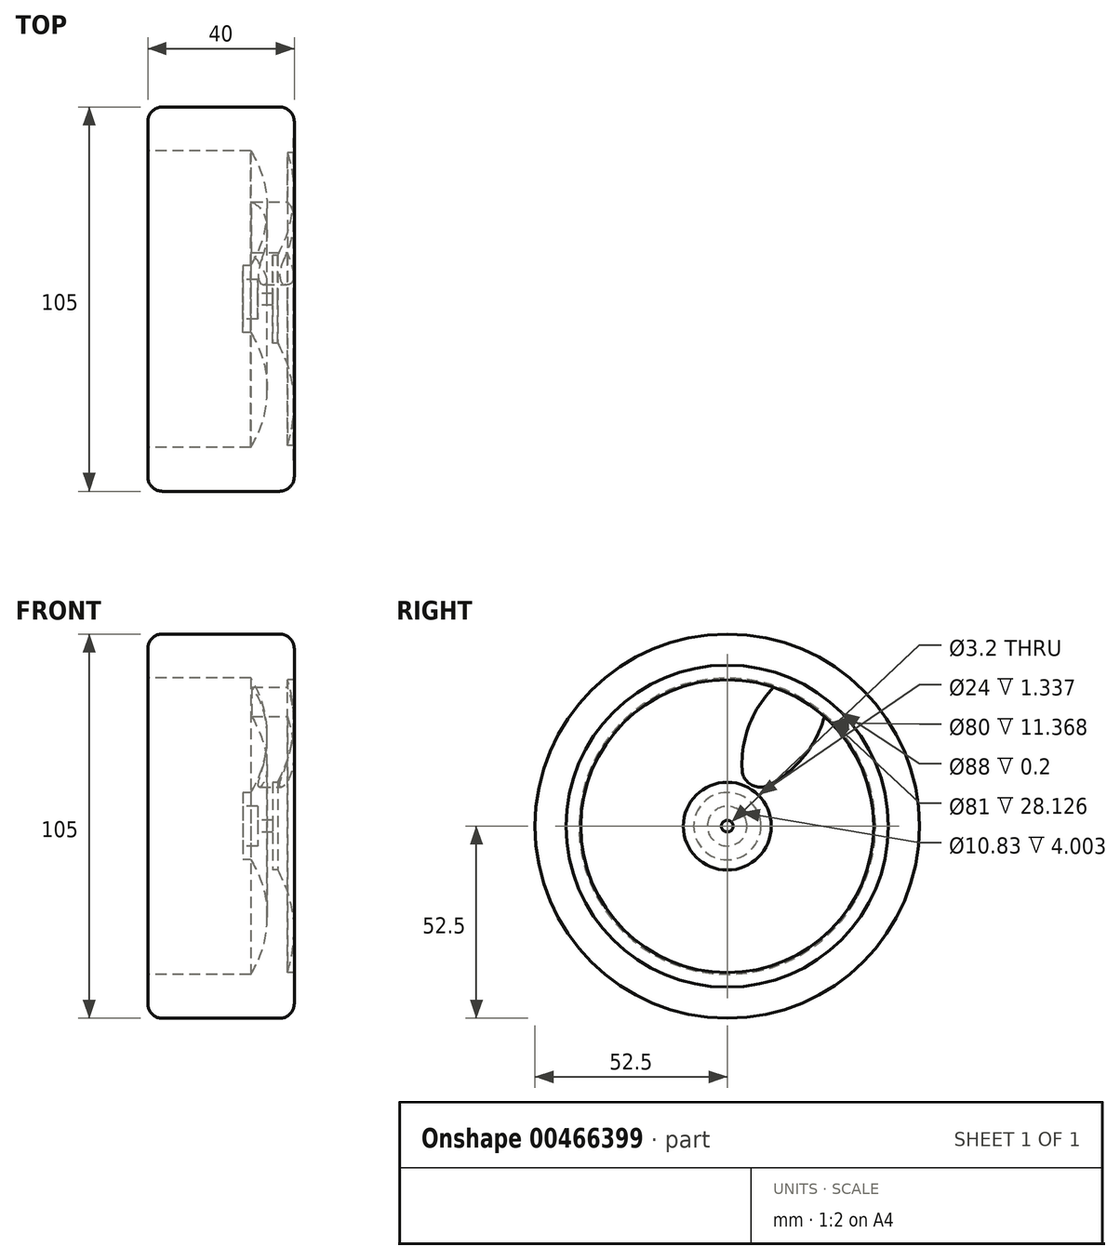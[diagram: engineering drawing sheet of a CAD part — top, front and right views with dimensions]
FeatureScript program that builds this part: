
annotation { "Feature Type Name" : "Feature", "Feature Type Description" : "" }
export const myFeature = defineFeature(function(context is Context, id is Id, definition is map)
    precondition{}
    {
        {
            var Q0;
            Q0=qCreatedBy(makeId("Front.planeOp"),FACE);
            var sketch = newSketch(context, id + "F0", { "sketchPlane" : qUnion([Q0])});
            skLineSegment(sketch, "E0", {"start": v(0, 52.5) * mm, "end": v(40, 52.5) * mm});
            skLineSegment(sketch, "E1", {"start": v(40, 52.5) * mm, "end": v(40, 44) * mm});
            skLineSegment(sketch, "E2", {"start": v(0, 52.5) * mm, "end": v(0, 40.5) * mm});
            skLineSegment(sketch, "E3", {"start": v(0, 40.5) * mm, "end": v(28.13, 40.5) * mm});
            skLineSegment(sketch, "E4", {"start": v(-66.92, 0) * mm, "end": v(78.57, 0) * mm, "construction": true});
            skLineSegment(sketch, "E5", {"start": v(26, 9.18) * mm, "end": v(26, 5.41) * mm});
            skLineSegment(sketch, "E6", {"start": v(26, 5.41) * mm, "end": v(30, 5.41) * mm});
            skLineSegment(sketch, "E7", {"start": v(30, 5.41) * mm, "end": v(30, 1.6) * mm});
            skLineSegment(sketch, "E8", {"start": v(30, 1.6) * mm, "end": v(34.12, 1.6) * mm});
            skLineSegment(sketch, "E9", {"start": v(34.12, 1.6) * mm, "end": v(34.12, 12) * mm});
            skLineSegment(sketch, "E10", {"start": v(26, 9.18) * mm, "end": v(28.13, 9.18) * mm});
            skLineSegment(sketch, "E11", {"start": v(39.8, 40) * mm, "end": v(38.14, 40) * mm});
            skLineSegment(sketch, "E12", {"start": v(34.12, 12) * mm, "end": v(35.45, 12) * mm});
            skArc(sketch, "E13.trimOffspring", {"start": v(35.45, 12) * mm, "mid": v(39.73, 25.72) * mm, "end": v(38.14, 40) * mm});
            skLineSegment(sketch, "E14", {"start": v(40, 44) * mm, "end": v(39.8, 44) * mm});
            skLineSegment(sketch, "E15", {"start": v(39.8, 44) * mm, "end": v(39.8, 40) * mm});
            skArc(sketch, "E16.trimOffspring", {"start": v(28.13, 9.18) * mm, "mid": v(32.62, 24.84) * mm, "end": v(28.13, 40.5) * mm});
            skSolve(sketch);
        }
        {
            var Q0;
            Q0 = qSketchRegion(id + "F0", true);
            var Q1;
            Q1=sQuery(id+"F0.wireOp",EDGE,"E4");
            revolve(context, id + "F1", {"entities" : qUnion([Q0]), "axis" : qUnion([Q1]), "revolveType" : RevolveType.FULL});
        }
        {
            var Q0;
            Q0=makeQuery(id+"F1.opRevolve","SWEPT_EDGE",EDGE,{"disambiguationData":[OSD([sQuery(id+"F0.wireOp",EDGE,"E0"),sQuery(id+"F0.wireOp",EDGE,"E1")])]});
            var Q1;
            Q1=makeQuery(id+"F1.opRevolve","SWEPT_EDGE",EDGE,{"disambiguationData":[OSD([sQuery(id+"F0.wireOp",EDGE,"E0"),sQuery(id+"F0.wireOp",EDGE,"E2")])]});
            fillet(context, id + "F2", {"entities" : qUnion([Q0, Q1]), "radius" : 4 * mm, "tangentPropagation" : true, "allowEdgeOverflow" : false});
        }
        {
            var Q0;
            Q0=makeQuery(id+"F1.opRevolve","SWEPT_FACE",FACE,{"disambiguationData":[OSD([sQuery(id+"F0.wireOp",EDGE,"E1")])]});
            var sketch = newSketch(context, id + "F3", { "sketchPlane" : qUnion([Q0])});
            skLineSegment(sketch, "E17", {"start": v(0, 0) * mm, "end": v(22, 38.1) * mm, "construction": true});
            skArc(sketch, "E18", {"start": v(4.04, 15.41) * mm, "mid": v(6.54, 11.32) * mm, "end": v(11.33, 11.2) * mm});
            skArc(sketch, "E19", {"start": v(26.52, 29.94) * mm, "mid": v(20, 34.64) * mm, "end": v(12.67, 37.94) * mm});
            skArc(sketch, "E20", {"start": v(12.67, 37.94) * mm, "mid": v(6, 27.58) * mm, "end": v(4.04, 15.41) * mm});
            skArc(sketch, "E21", {"start": v(11.33, 11.2) * mm, "mid": v(20.9, 18.98) * mm, "end": v(26.52, 29.94) * mm});
            skSolve(sketch);
        }
        {
            var Q0;
            Q0 = qSketchRegion(id + "F3", true);
            extrude(context, id + "F4", {"entities" : qUnion([Q0]), "operationType" : NewBodyOperationType.REMOVE, "endBound" : BoundingType.THROUGH_ALL, "oppositeDirection" : true, "depth" : 25 * mm, "offsetDistance" : 25 * mm});
        }
    });
